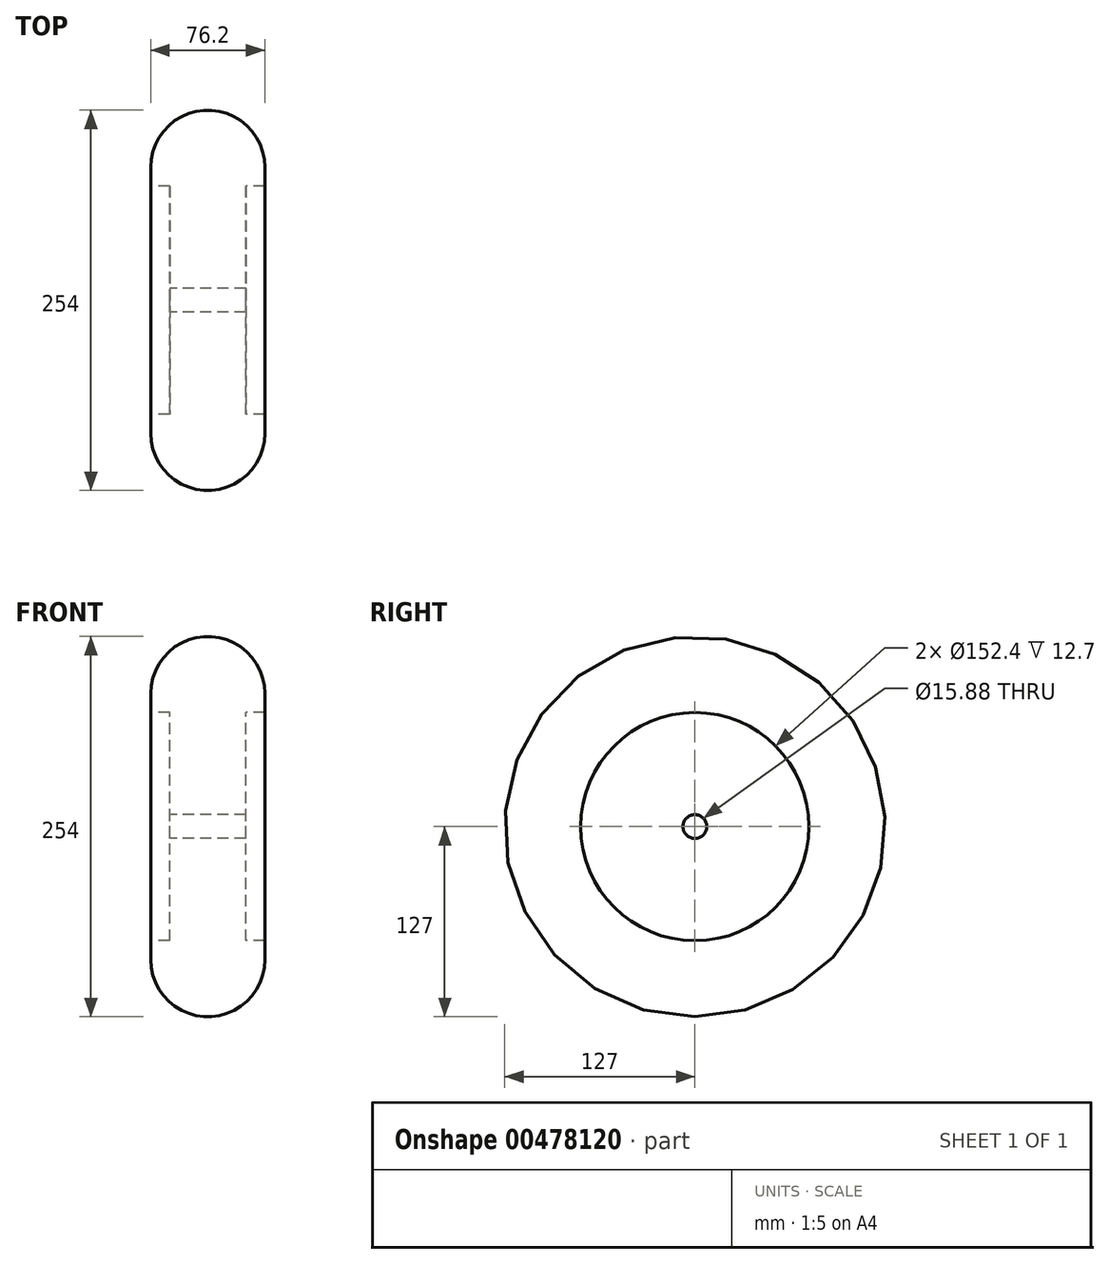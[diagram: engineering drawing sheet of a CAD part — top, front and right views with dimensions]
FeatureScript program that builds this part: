
annotation { "Feature Type Name" : "Feature", "Feature Type Description" : "" }
export const myFeature = defineFeature(function(context is Context, id is Id, definition is map)
    precondition{}
    {
        {
            var Q0;
            Q0=qCreatedBy(makeId("Right.planeOp"),FACE);
            var sketch = newSketch(context, id + "F0", { "sketchPlane" : qUnion([Q0])});
            skCircle(sketch, "E0", {"center": v(0, 0) * mm, "radius": 127 * mm});
            skCircle(sketch, "E1", {"center": v(0, 0) * mm, "radius": 7.94 * mm});
            skCircle(sketch, "E2", {"center": v(0, 0) * mm, "radius": 76.2 * mm});
            skSolve(sketch);
        }
        {
            var Q0;
            Q0=makeQuery(id+"F0.imprint","IMPRINT",FACE,{"disambiguationData":[TD([[makeQuery(id+"F0.imprint","IMPRINT",EDGE,{"derivedFrom":sQuery(id+"F0.wireOp",EDGE,"E0")}),1.0]])]});
            extrude(context, id + "F1", {"entities" : qUnion([Q0]), "depth" : 76.2 * mm, "symmetric" : true});
        }
        {
            var Q0;
            Q0=makeQuery(id+"F1.opExtrude","CAP_EDGE",EDGE,{"disambiguationData":[OSD([sQuery(id+"F0.wireOp",EDGE,"E0")])],"isStart":false});
            var Q1;
            Q1=makeQuery(id+"F1.opExtrude","CAP_EDGE",EDGE,{"disambiguationData":[OSD([sQuery(id+"F0.wireOp",EDGE,"E0")])],"isStart":true});
            fillet(context, id + "F2", {"entities" : qUnion([Q0, Q1]), "radius" : 38.1 * mm, "tangentPropagation" : true, "allowEdgeOverflow" : false});
        }
        {
            var Q0;
            Q0=makeQuery(id+"F0.imprint","IMPRINT",FACE,{"disambiguationData":[TD([[makeQuery(id+"F0.imprint","IMPRINT",EDGE,{"derivedFrom":sQuery(id+"F0.wireOp",EDGE,"E1")}),-1.0]])]});
            extrude(context, id + "F3", {"entities" : qUnion([Q0]), "operationType" : NewBodyOperationType.ADD, "depth" : 50.8 * mm, "offsetDistance" : 25.4 * mm, "symmetric" : true});
        }
    });
